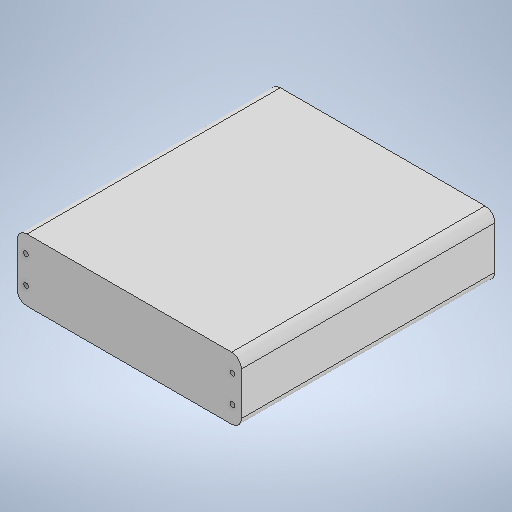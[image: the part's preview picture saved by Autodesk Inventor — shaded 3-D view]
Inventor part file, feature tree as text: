
AUTODESK INVENTOR PART (.ipt)
format: ipt  version: 2025.1 (Build 291241000, 241)  size: 223,744 bytes
history: native  units: mm
features: sketch x1, extrude x1, hole x1
ambient origin geometry x8: Origin, YZ Plane, XZ Plane, XY Plane, X Axis, Y Axis, Z Axis, Center Point
bodies: Volumenkörper1 (feature_tree)
feature tree (3):
  sketch  "Skizze1"  dims[d0=115.0mm d1=32.0mm d2=5.0mm d3=3.0mm d4=7.0mm d5=53.0mm d6=130.0mm d7=0.0mm d8=2.459mm d9=10.0mm d10=6.3mm d11=2.0mm d12=90.0deg d13=12.0mm d14=20.594885mm]
  extrude  "Extrusion1"  Depth=32.0mm
  hole  "Bohrung1"  [1 undecoded]
note: 1 required parameter value undecoded (feature->parameter linkage not recoverable at this tier; creation-order binding heuristic only, values carry confidence <= 0.55)
